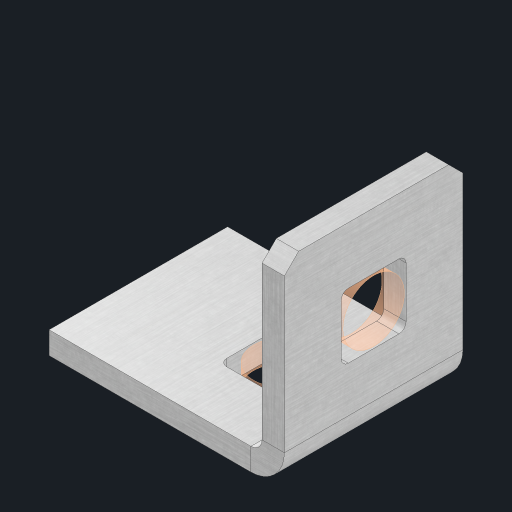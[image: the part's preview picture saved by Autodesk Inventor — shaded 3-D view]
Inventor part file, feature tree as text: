
AUTODESK INVENTOR PART (.ipt)
format: ipt  version: 2023 (Build 270158000, 158)  size: 524,288 bytes
history: native  units: in
note: dims shown in document units (in); Inventor stores cm internally (conversion verified against a paired STEP export)
features: other x75, extrude x69, sheet_metal_op x10, sketch x8, mirror x1, pattern_linear x1, chamfer x1
ambient origin geometry x8: Origin, YZ Plane, XZ Plane, XY Plane, X Axis, Y Axis, Z Axis, Center Point
bodies: Solid1 (feature_tree), Body (feature_tree)
feature tree (165):
  other  "Flange Pattern Plane"
  sheet_metal_op  "Flange Pattern"
  sheet_metal_op  "Body Pattern"
  other  "Arc Length"
  mirror  "Notch Mirror"
  pattern_linear  "Notch Pattern"  Spacing1=0.25in  [1 undecoded]
  chamfer  "End Chamfer"
  extrude  "Half Cut"  Depth=0.0625in
  sketch  "Sketch1"  dims[d0=1.5in]
  other  "Plate1"
  sketch  "Sketch2"  dims[d1=0.5in]
  other  "Plate2"
  sheet_metal_op  "Bend1"
  sheet_metal_op  "Corner1"
  sketch  "Sketch3"  dims[d2=0.0625in]
  other  "Flange Pattern Sketch"
  sketch  "Sketch7"  dims[d3=0.0625in]
  other  "Srf1"
  other  "Srf2"
  sketch  "Sketch8"  dims[d4=0.0312in]
  sketch  "Sketch9"  dims[d5=0.125in]
  other  "Srf91"
  sheet_metal_op  "Body Pattern Sketch"
  other  "Srf92"
  sketch  "Sketch13"  dims[d6=0.0625in]
  sketch  "Sketch14"  dims[d7=0.5in d8=90.0deg d9=0.0312in d10=0.25in d11=0.0625in d12=0.0625in d16=0.182in d17=0.02in d18=0.0625in d19=0.0in d20=0.25in d21=0.25in d46=0.172in d47=1.0in d48=0.0in d49=0.182in d50=0.02in d51=0.25in d52=0.25in d53=0.0625in d54=0.0in d55=0.172in d56=1.0in d57=0.0in d60=0.3937in d62=0.5in d63=0.3937in d65=0.5in d85=0.1473in d86=0.1782in d88=0.04in d89=0.0625in d90=0.0in d91=0.04in d92=0.0491in d95=2.5in d96=0.04in d97=0.25in d98=45.0deg d101=0.0in d102=2.497in d131=0.5in d132=0.3937in d134=0.5in d139=0.5in]
  other  "Srf856"
  other  "Srf1310"
  other  "Srf1311"
  other  "Srf1312"
  other  "Srf1376"
  other  "Srf1377"
  other  "Srf1728"
  other  "Srf1755"
  other  "Srf1878"
  other  "Srf1879"
  other  "Srf1880"
  other  "Srf1881"
  other  "Srf1882"
  other  "Srf1883"
  other  "Srf1884"
  other  "Srf1885"
  other  "Srf1886"
  other  "Srf1887"
  other  "Srf1888"
  other  "Srf1889"
  other  "Srf1890"
  other  "Srf1891"
  other  "Srf1892"
  other  "Srf1893"
  other  "Srf1894"
  other  "Srf1895"
  other  "Srf1896"
  other  "Srf1897"
  other  "Srf1898"
  other  "Srf1899"
  other  "Srf1900"
  other  "Srf1901"
  other  "Srf1902"
  other  "Srf1903"
  other  "Srf1904"
  other  "Srf1905"
  other  "Srf1906"
  other  "Srf1942"
  other  "Srf1943"
  other  "Srf1944"
  other  "Srf1945"
  other  "Srf1946"
  other  "Srf1947"
  other  "Srf1948"
  other  "Srf1949"
  other  "Srf1950"
  other  "Srf1951"
  other  "Srf1952"
  other  "Srf1953"
  other  "Srf1954"
  other  "Srf1955"
  other  "Srf1956"
  other  "Srf1957"
  other  "Srf1958"
  other  "Srf1959"
  other  "Srf1960"
  other  "Srf1961"
  other  "Srf1962"
  other  "Srf1963"
  other  "Srf1964"
  other  "Srf1965"
  other  "Srf1966"
  other  "Srf1967"
  other  "Srf1968"
  other  "Srf1969"
  other  "Srf1970"
  sheet_metal_op  "Flange Stamp"
  sheet_metal_op  "Flange Circle"
  sheet_metal_op  "Body Stamp"
  sheet_metal_op  "Body Circle"
  sheet_metal_op  "Notch"
  extrude  "ExtrusionSrf2"  Depth=0.0625in
  extrude  "ExtrusionSrf92"  Depth=0.182in
  extrude  "ExtrusionSrf856"  Depth=0.02in
  extrude  "ExtrusionSrf1310"  Depth=0.0625in
  extrude  "ExtrusionSrf1311"  TaperAngle=0.0deg  [1 undecoded]
  extrude  "ExtrusionSrf1312"  Depth=0.25in
  extrude  "ExtrusionSrf1376"  Depth=0.25in
  extrude  "ExtrusionSrf1377"  Depth=0.5in
  extrude  "ExtrusionSrf1728"  Depth=0.5in TaperAngle=0.0deg
  extrude  "ExtrusionSrf1755"  Depth=0.182in
  extrude  "ExtrusionSrf1878"  Depth=0.02in
  extrude  "ExtrusionSrf1879"  Depth=0.25in
  extrude  "ExtrusionSrf1880"  Depth=0.25in
  extrude  "ExtrusionSrf1881"  Depth=0.0625in
  extrude  "ExtrusionSrf1882"  TaperAngle=0.0deg  [1 undecoded]
  extrude  "ExtrusionSrf1883"  Depth=0.5in
  extrude  "ExtrusionSrf1884"  Depth=0.5in TaperAngle=0.0deg
  extrude  "ExtrusionSrf1885"  Depth=0.3937in
  extrude  "ExtrusionSrf1886"  Depth=0.5in
  extrude  "ExtrusionSrf1887"  Depth=0.5in
  extrude  "ExtrusionSrf1888"  Depth=0.5in
  extrude  "ExtrusionSrf1889"  Depth=0.5in
  extrude  "ExtrusionSrf1890"  Depth=0.0625in
  extrude  "ExtrusionSrf1891"  TaperAngle=0.0deg  [1 undecoded]
  extrude  "ExtrusionSrf1892"  Depth=0.5in
  extrude  "ExtrusionSrf1893"  Depth=0.5in
  extrude  "ExtrusionSrf1894"  Depth=0.5in
  extrude  "ExtrusionSrf1895"  Depth=0.25in TaperAngle=45.0deg
  extrude  "ExtrusionSrf1896"  TaperAngle=0.0deg  [1 undecoded]
  extrude  "ExtrusionSrf1897"  Depth=0.5in
  extrude  "ExtrusionSrf1898"  Depth=0.5in
  extrude  "ExtrusionSrf1899"  Depth=0.3937in
  extrude  "ExtrusionSrf1900"  Depth=0.5in
  extrude  "ExtrusionSrf1901"  Depth=0.5in
  extrude  "ExtrusionSrf1902"  [1 undecoded]
  extrude  "ExtrusionSrf1903"  [1 undecoded]
  extrude  "ExtrusionSrf1904"  [1 undecoded]
  extrude  "ExtrusionSrf1905"  [1 undecoded]
  extrude  "ExtrusionSrf1906"  [1 undecoded]
  extrude  "ExtrusionSrf1942"  [1 undecoded]
  extrude  "ExtrusionSrf1943"  [1 undecoded]
  extrude  "ExtrusionSrf1944"  [1 undecoded]
  extrude  "ExtrusionSrf1945"  [1 undecoded]
  extrude  "ExtrusionSrf1946"  [1 undecoded]
  extrude  "ExtrusionSrf1947"  [1 undecoded]
  extrude  "ExtrusionSrf1948"  [1 undecoded]
  extrude  "ExtrusionSrf1949"  [1 undecoded]
  extrude  "ExtrusionSrf1950"  [1 undecoded]
  extrude  "ExtrusionSrf1951"  [1 undecoded]
  extrude  "ExtrusionSrf1952"  [1 undecoded]
  extrude  "ExtrusionSrf1953"  [1 undecoded]
  extrude  "ExtrusionSrf1954"  [1 undecoded]
  extrude  "ExtrusionSrf1955"  [1 undecoded]
  extrude  "ExtrusionSrf1956"  [1 undecoded]
  extrude  "ExtrusionSrf1957"  [1 undecoded]
  extrude  "ExtrusionSrf1958"  [1 undecoded]
  extrude  "ExtrusionSrf1959"  [1 undecoded]
  extrude  "ExtrusionSrf1960"  [1 undecoded]
  extrude  "ExtrusionSrf1961"  [1 undecoded]
  extrude  "ExtrusionSrf1962"  [1 undecoded]
  extrude  "ExtrusionSrf1963"  [1 undecoded]
  extrude  "ExtrusionSrf1964"  [1 undecoded]
  extrude  "ExtrusionSrf1965"  [1 undecoded]
  extrude  "ExtrusionSrf1966"  [1 undecoded]
  extrude  "ExtrusionSrf1967"  [1 undecoded]
  extrude  "ExtrusionSrf1968"  [1 undecoded]
  extrude  "ExtrusionSrf1969"  [1 undecoded]
  extrude  "ExtrusionSrf1970"  [1 undecoded]
note: 39 required parameter values undecoded (feature->parameter linkage not recoverable at this tier; creation-order binding heuristic only, values carry confidence <= 0.55)
